# Revit family: IS_Ceratherm100_A5619_BIM_DE
name_source: partatom
category: Plumbing Fixtures
revit_build: Autodesk Revit MEP 2016 (Build: 20161004_0715(x64)
units: mm (PartAtom-declared; Revit-internal decimal feet)

## family parameters
Always vertical = No
Cut with Voids When Loaded = No
OmniClass Number = 23.45.55.17
OmniClass Title = Mixing Faucets
Part Type = Normal
Room Calculation Point = No
Round Connector Dimension = Use Diameter
Shared = No
Work Plane-Based = No

## types (1)
- A5619AA - CERATHERM100 thermostatic build-in bath shower mixer
    Accessories = www.idealstandard.de\ersatzteile
    AreaUnits = millimeters
    AssetType = Fixed
    BIMObjectName = ISI_IdealStandard_BathTaps_Ceratherm100New_A5619AA
    BIMobject category = Taps & Mixers
    BOSUseNativeGeometries = 1
    BarCode = 4015413313315
    Brand = Ideal Standard
    Brand url = http://www.idealstandard.co.uk
    CodePerformance = 0
    Color = Chrome
    ConnectionType = Plumbing
    Cost = 0 $
    CurrencyUnit = €
    CurrentRevision = 1
    Date of publishing = 2017_11_21
    Description = A5619AA CERATHERM100 thermostatic build-in bath shower mixer
    DurationUnit = year
    EAN code = https://4015413313315
    Edition number = 1
    ExpectedLife = 25
    FaucetFunction = thermostatic
    FaucetOperation = leverhandle
    FaucetType = pillar
    Features = CERATHERM100 thermostatic build-in bath shower mixer
    Finish = Chrome
    IFC Classification = Sanitary Terminal
    IfcExportAs = IfcValveType
    IfcExportType = FAUCET
    Installation instructions = http://www.idealstandard.de
    InstallationInstructions = www.idealstandard.de\produkte
    LinearUnits = millimeters
    MainColor = Chrome
    MaintenanceInformation = www.idealstandard.de\produkte
    Manufacturer name = Ideal Standard
    ManufacturerURL = www.idealstandard.com
    Material = Brass
    Material main = Brass
    Model = A5619AA
    ModelNumber = A5619AA
    ModelReference = A5619AA CERATHERM100 thermostatic build-in bath shower mixer
    NBS Reference Code = 35-06-07
    NBS Reference Description = Bath Water Supply Fittings
    Name = BathTaps_Ceratherm100New_A5619AA_IdealStandard
    NettWeight = 1,668 kg
    Nominal height = 163
    Nominal width = 163
    NominalDepth = 82 mm  [stored 0.269029 ft]
    NominalHeight = 163 mm  [stored 0.534777 ft]
    NominalLength = 82 mm  [stored 0.269029 ft]
    NominalWidth = 163 mm  [stored 0.534777 ft]
    OmniClass Code = 23-31 11 00
    OmniClass Description = Faucets
    Product Guid = e2c9f51e-9682-4e33-a2ba-f1895526ae98
    Product SKU = A5619
    Product data url = https://bimobject.com
    Product family = CERATHERM 100 NEW
    Product group = Bath & Shower Mixer
    Product name = CERATHERM100 thermostatic build-in bath shower mixer
    Product url = http://www.idealstandard.de
    ProductInformation = www.idealstandard.de/produkte
    QR code = http://bimobject.com
    Shape = Sculptured
    Size = 163 x 82 x 163mm
    Space = Internal
    SpareParts = www.idealstandard.de/ersatzteile
    Technical description = http://www.idealstandard.de
    TestPressure = 10bar
    URL = www.idealstandard.com
    Uniclass 1.4 Code = L8212
    Uniclass 1.4 Description = Fittings
    Uniclass 2.0 Code = PR-35-06-07
    Uniclass 2.0 Description = Bath Water Supply Fittings
    Uniclass 2015 Code = Pr_40_20_87_07
    Uniclass 2015 Name = Bath manual water supply sets
    Uniclass2015Code = Pr_40_20_87_07
    Uniclass2015Title = Bath manual water supply sets
    Uniclass2015Version = Products v1.1
    ValveOperation = lever
    Version = 1
    VolumeUnits = Litres
    Weight Net (Kg) = 1.67
    WorkingPressure = 1-5 Bar

note: [stored X ft] marks values corroborated as IEEE doubles in the binary element streams (Revit-internal decimal feet)

## geometry (parser evidence)
native form markers: Blend x4, Sweep x1
no freeform markers — native parametric forms only
